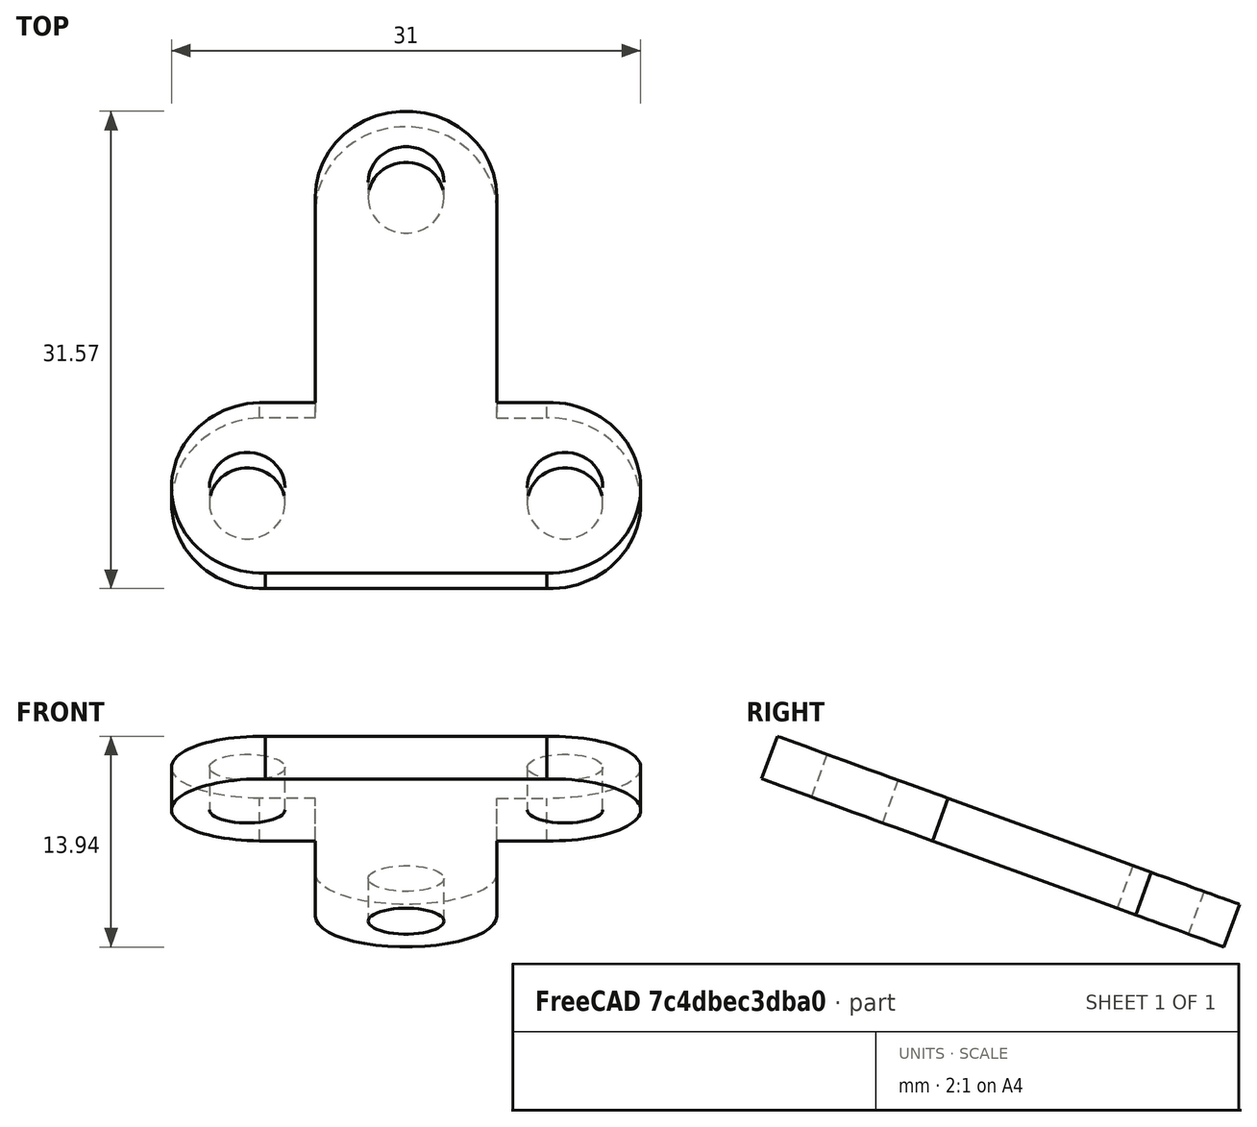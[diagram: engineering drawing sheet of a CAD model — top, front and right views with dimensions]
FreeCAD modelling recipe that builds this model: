
FCSTD DOCUMENT  (FreeCAD 0.18R16110 (Git))
Label: armscrew
License: All rights reserved
LicenseURL: http://en.wikipedia.org/wiki/All_rights_reserved
objects: Sketcher::SketchObject×1, Part::Extrusion×1
note: 2 computed .brp shape members not serialized (recipe doc carries the construction recipe); baked Part::Feature solids carry a one-line shape summary decoded from their .brp

FEATURE [Sketcher::SketchObject] Sketch001
  MapMode = 5
  Placement = pos=(0,72.8427,200.134) rot=(-1,0,0;0.349066rad)
  sketch-geometry (15):
    g0: ArcOfCircle CenterX=0 CenterY=20.5 CenterZ=0 NormalX=0 NormalY=0 NormalZ=1 AngleXU=0 Radius=6 StartAngle=6.24985 EndAngle=9.45812
    g1: Circle CenterX=0 CenterY=21.5 CenterZ=0 NormalX=0 NormalY=0 NormalZ=1 AngleXU=0 Radius=2.5
    g2: LineSegment StartX=-5.99667 StartY=20.3 StartZ=0 EndX=-5.99667 EndY=17 EndZ=0
    g3: LineSegment StartX=5.99667 StartY=20.3 StartZ=0 EndX=5.99667 EndY=17 EndZ=0
    g4: LineSegment StartX=-5.99667 StartY=17 StartZ=0 EndX=-5.99667 EndY=6 EndZ=0
    g5: LineSegment StartX=5.99667 StartY=17 StartZ=0 EndX=5.99667 EndY=6 EndZ=0
    g6: LineSegment StartX=-5.99667 StartY=6 StartZ=0 EndX=-9.7 EndY=6 EndZ=0
    g7: LineSegment StartX=5.99667 StartY=6 StartZ=0 EndX=9.3 EndY=6 EndZ=0
    g8: LineSegment StartX=-9.3 StartY=-6 StartZ=0 EndX=-6 EndY=-6 EndZ=0
    g9: LineSegment StartX=-6 StartY=-6 StartZ=0 EndX=6 EndY=-6 EndZ=0
    g10: LineSegment StartX=6 StartY=-6 StartZ=0 EndX=9.3 EndY=-6 EndZ=0
    g11: ArcOfCircle CenterX=-9.5 CenterY=0 CenterZ=0 NormalX=0 NormalY=0 NormalZ=1 AngleXU=0 Radius=6.00333 StartAngle=1.60412 EndAngle=4.74571
    g12: ArcOfCircle CenterX=9.5 CenterY=0 CenterZ=0 NormalX=0 NormalY=0 NormalZ=1 AngleXU=0 Radius=6.00333 StartAngle=4.67907 EndAngle=7.8873
    g13: Circle CenterX=-10.5 CenterY=0 CenterZ=0 NormalX=0 NormalY=0 NormalZ=1 AngleXU=0 Radius=2.5
    g14: Circle CenterX=10.5 CenterY=0 CenterZ=0 NormalX=0 NormalY=0 NormalZ=1 AngleXU=0 Radius=2.5
  constraints (48):
    c: PointOnObject(g0,g-2)
    c: Radius(g0) = 6
    c: Radius(g1) = 2.5
    c: Coincident(g2,g0)
    c: Vertical(g2)
    c: Coincident(g3,g0)
    c: Vertical(g3)
    c: PointOnObject(g1,g-2)
    c: DistanceY(g1) = 21.5
    c: DistanceY(g2) = 17
    c: DistanceY(g3) = 17
    c: Coincident(g4,g2)
    c: Vertical(g4)
    c: Coincident(g5,g3)
    c: Vertical(g5)
    c: DistanceY(g5) = 6
    c: Distance(g2) = 3.3
    c: Distance(g3) = 3.3
    c: Coincident(g6,g4)
    c: Horizontal(g6)
    c: Coincident(g7,g5)
    c: Horizontal(g7)
    c: Horizontal(g8)
    c: DistanceX(g8) = -6
    c: Distance(g8) = 3.3
    c: Coincident(g9,g8)
    c: Horizontal(g9)
    c: DistanceX(g9) = 6
    c: Coincident(g10,g9)
    c: Horizontal(g10)
    c: DistanceX(g10) = 9.3
    c: DistanceX(g7) = 9.3
    c: DistanceY(g4) = 6
    c: DistanceY(g8) = -6
    c: PointOnObject(g11,g-1)
    c: Coincident(g11,g6)
    c: Coincident(g11,g8)
    c: Coincident(g12,g7)
    c: Coincident(g12,g10)
    c: PointOnObject(g13,g-1)
    c: DistanceX(g13) = -10.5
    c: Radius(g13) = 2.5
    c: PointOnObject(g14,g-1)
    c: DistanceX(g14) = 10.5
    c: Radius(g14) = 2.5
    c: DistanceY(g0) = 20.5
    c: DistanceX(g11) = -9.5
    c: DistanceX(g12) = 9.5
FEATURE [Part::Extrusion] Extrude
  Base = -> Sketch001
  Dir = (0,0.34202,0.939693)
  DirMode = 2
  FaceMakerClass = Part::FaceMakerBullseye
  LengthFwd = 3
  LengthRev = 0
  Solid = true
  Symmetric = false
